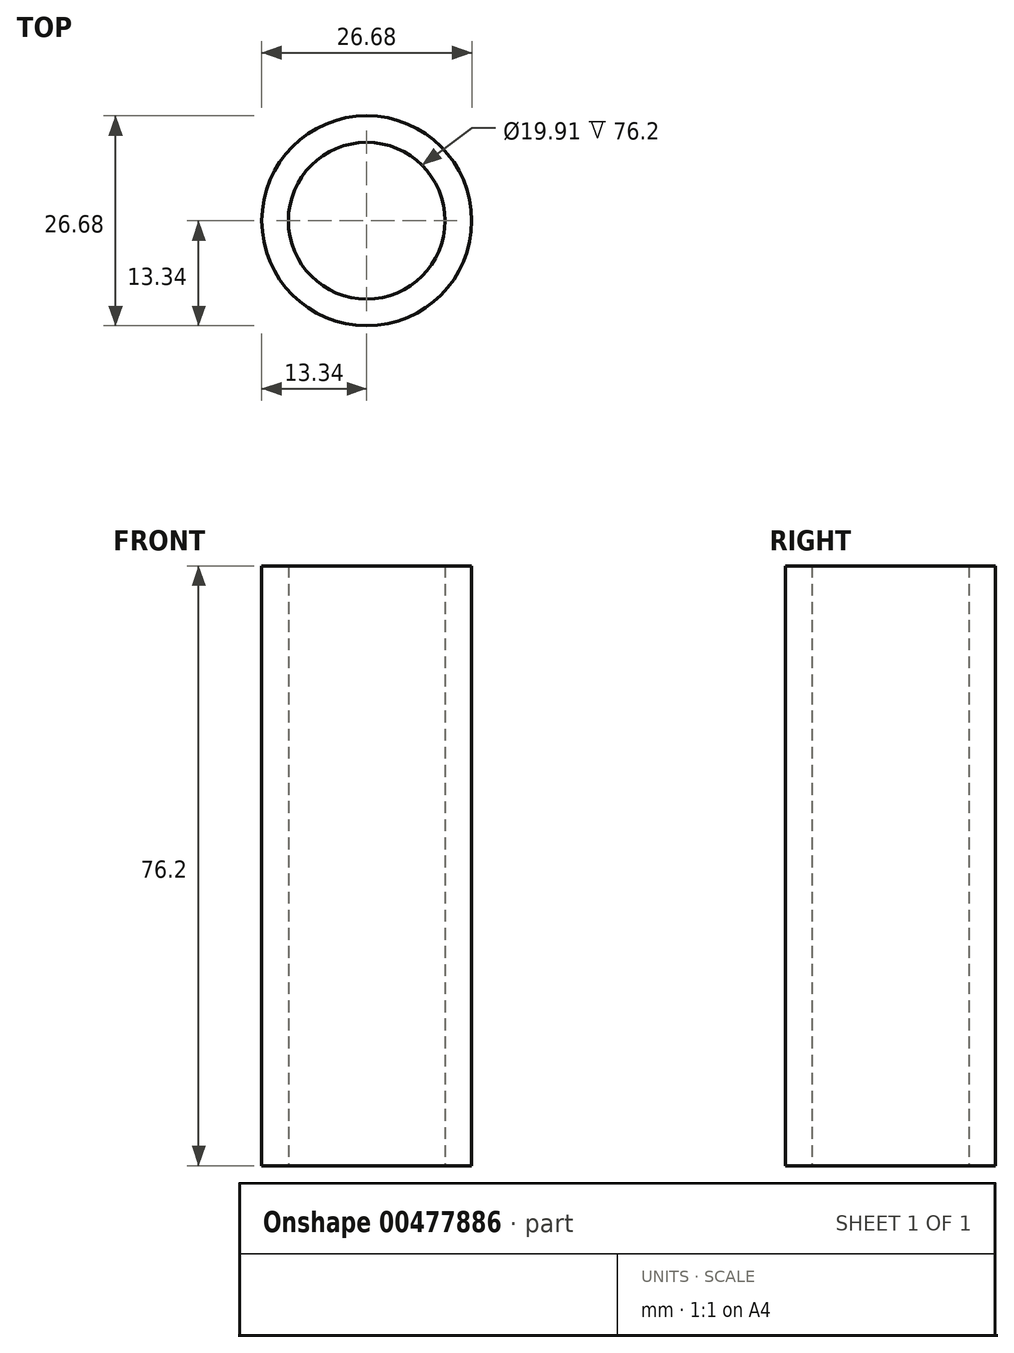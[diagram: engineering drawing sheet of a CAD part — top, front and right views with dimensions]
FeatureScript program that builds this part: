
annotation { "Feature Type Name" : "Feature", "Feature Type Description" : "" }
export const myFeature = defineFeature(function(context is Context, id is Id, definition is map)
    precondition{}
    {
        {
            var Q0;
            Q0=qCreatedBy(makeId("Top.planeOp"),FACE);
            var sketch = newSketch(context, id + "F0", { "sketchPlane" : qUnion([Q0])});
            skCircle(sketch, "E0", {"center": v(0, 0) * mm, "radius": 9.96 * mm});
            skCircle(sketch, "E1", {"center": v(0, 0) * mm, "radius": 13.34 * mm});
            skLineSegment(sketch, "E2", {"start": v(9.96, 0) * mm, "end": v(13.34, 0) * mm, "construction": true});
            skSolve(sketch);
        }
        {
            var Q0;
            Q0=makeQuery(id+"F0.imprint","IMPRINT",FACE,{"disambiguationData":[TD([[makeQuery(id+"F0.imprint","IMPRINT",EDGE,{"derivedFrom":sQuery(id+"F0.wireOp",EDGE,"E0")}),-1.0]])]});
            extrude(context, id + "F1", {"entities" : qUnion([Q0]), "depth" : 76.2 * mm, "offsetDistance" : 25.4 * mm});
        }
    });
